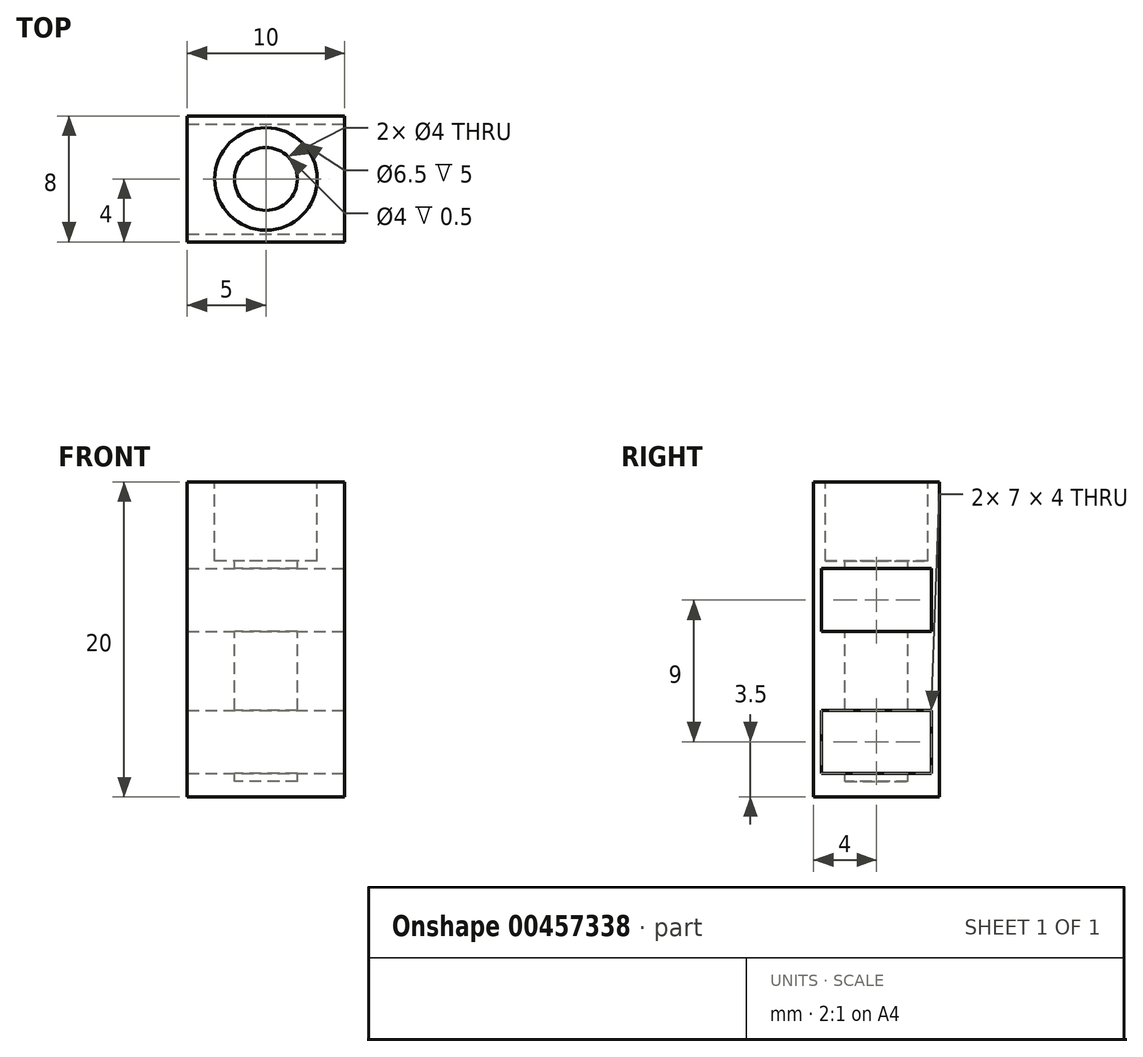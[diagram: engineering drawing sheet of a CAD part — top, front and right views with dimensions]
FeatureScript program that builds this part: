
annotation { "Feature Type Name" : "Feature", "Feature Type Description" : "" }
export const myFeature = defineFeature(function(context is Context, id is Id, definition is map)
    precondition{}
    {
        {
            var Q0;
            Q0=qCreatedBy(makeId("Front.planeOp"),FACE);
            var sketch = newSketch(context, id + "F0", { "sketchPlane" : qUnion([Q0])});
            skLineSegment(sketch, "E0.bottom", {"start": v(-7.5, 10) * mm, "end": v(7.5, 10) * mm});
            skLineSegment(sketch, "E0.top", {"start": v(-7.5, -10) * mm, "end": v(7.5, -10) * mm});
            skLineSegment(sketch, "E0.left", {"start": v(-7.5, 10) * mm, "end": v(-7.5, -10) * mm});
            skLineSegment(sketch, "E0.right", {"start": v(7.5, 10) * mm, "end": v(7.5, -10) * mm});
            skPoint(sketch, "E0.middle", {"position": v(0, 0) * mm});
            skSolve(sketch);
        }
        {
            var Q0;
            Q0 = qSketchRegion(id + "F0", true);
            extrude(context, id + "F1", {"entities" : qUnion([Q0]), "endBound" : BoundingType.SYMMETRIC, "depth" : 8 * mm});
        }
        {
            var Q0;
            Q0=makeQuery(id+"F1.opExtrude","SWEPT_FACE",FACE,{"disambiguationData":[OSD([sQuery(id+"F0.wireOp",EDGE,"E0.bottom")])]});
            var sketch = newSketch(context, id + "F2", { "sketchPlane" : qUnion([Q0])});
            skCircle(sketch, "E1", {"center": v(-2.5, 0) * mm, "radius": 2 * mm});
            skPoint(sketch, "E1.centerSnap0", {"position": v(-7.5, 0) * mm});
            skSolve(sketch);
        }
        {
            var Q0;
            Q0 = qSketchRegion(id + "F2", true);
            extrude(context, id + "F3", {"entities" : qUnion([Q0]), "operationType" : NewBodyOperationType.REMOVE, "oppositeDirection" : true, "depth" : 19 * mm});
        }
        {
            var Q0;
            Q0=makeQuery(id+"F1.opExtrude","SWEPT_FACE",FACE,{"disambiguationData":[OSD([sQuery(id+"F0.wireOp",EDGE,"E0.bottom")])]});
            var sketch = newSketch(context, id + "F4", { "sketchPlane" : qUnion([Q0])});
            skCircle(sketch, "E2", {"center": v(-2.5, 0) * mm, "radius": 3.25 * mm});
            skSolve(sketch);
        }
        {
            var Q0;
            Q0=makeQuery(id+"F4.imprint","IMPRINT",FACE,{"disambiguationData":[TD([[makeQuery(id+"F4.imprint","IMPRINT",EDGE,{"derivedFrom":sQuery(id+"F4.wireOp",EDGE,"E2")}),1.0]])]});
            extrude(context, id + "F5", {"entities" : qUnion([Q0]), "operationType" : NewBodyOperationType.REMOVE, "oppositeDirection" : true, "depth" : 5 * mm});
        }
        {
            var Q0;
            Q0=makeQuery(id+"F1.opExtrude","SWEPT_FACE",FACE,{"disambiguationData":[OSD([sQuery(id+"F0.wireOp",EDGE,"E0.right")])]});
            var sketch = newSketch(context, id + "F6", { "sketchPlane" : qUnion([Q0])});
            skLineSegment(sketch, "E3.bottom", {"start": v(3.5, -4.5) * mm, "end": v(-3.5, -4.5) * mm});
            skLineSegment(sketch, "E3.top", {"start": v(3.5, -8.5) * mm, "end": v(-3.5, -8.5) * mm});
            skLineSegment(sketch, "E3.left", {"start": v(3.5, -4.5) * mm, "end": v(3.5, -8.5) * mm});
            skLineSegment(sketch, "E3.right", {"start": v(-3.5, -4.5) * mm, "end": v(-3.5, -8.5) * mm});
            skPoint(sketch, "E3.middle", {"position": v(0, -6.5) * mm});
            skPoint(sketch, "E4", {"position": v(0, -10) * mm});
            skLineSegment(sketch, "E5.0.1.0", {"start": v(3.5, 4.5) * mm, "end": v(-3.5, 4.5) * mm});
            skLineSegment(sketch, "E5.0.1.1", {"start": v(-3.5, 4.5) * mm, "end": v(-3.5, 0.5) * mm});
            skLineSegment(sketch, "E5.0.1.2", {"start": v(3.5, 0.5) * mm, "end": v(-3.5, 0.5) * mm});
            skLineSegment(sketch, "E5.0.1.3", {"start": v(3.5, 4.5) * mm, "end": v(3.5, 0.5) * mm});
            skPoint(sketch, "E5.0.1.4", {"position": v(0, 2.5) * mm});
            skLineSegment(sketch, "E5.direction1", {"start": v(-3.5, -4.5) * mm, "end": v(22, -4.5) * mm, "construction": true});
            skLineSegment(sketch, "E5.direction2", {"start": v(-3.5, -4.5) * mm, "end": v(-3.5, 4.5) * mm, "construction": true});
            skSolve(sketch);
        }
        {
            var Q0;
            Q0=makeQuery(id+"F6.imprint","IMPRINT",FACE,{"disambiguationData":[TD([[makeQuery(id+"F6.imprint","IMPRINT",EDGE,{"derivedFrom":sQuery(id+"F6.wireOp",EDGE,"E5.0.1.0")}),1.0]])]});
            var Q1;
            Q1=makeQuery(id+"F6.imprint","IMPRINT",FACE,{"disambiguationData":[TD([[makeQuery(id+"F6.imprint","IMPRINT",EDGE,{"derivedFrom":sQuery(id+"F6.wireOp",EDGE,"E3.bottom")}),1.0]])]});
            extrude(context, id + "F7", {"entities" : qUnion([Q0, Q1]), "operationType" : NewBodyOperationType.REMOVE, "endBound" : BoundingType.THROUGH_ALL, "oppositeDirection" : true, "depth" : 14 * mm});
        }
        {
            var Q0;
            Q0=makeQuery(id+"F1.opExtrude","CAP_FACE",FACE,{"disambiguationData":[OSD([sQuery(id+"F0.wireOp",EDGE,"E0.bottom"),sQuery(id+"F0.wireOp",EDGE,"E0.top"),sQuery(id+"F0.wireOp",EDGE,"E0.left"),sQuery(id+"F0.wireOp",EDGE,"E0.right")])],"isStart":false});
            var sketch = newSketch(context, id + "F8", { "sketchPlane" : qUnion([Q0])});
            skLineSegment(sketch, "E6.bottom", {"start": v(7.5, 10) * mm, "end": v(2.5, 10) * mm});
            skLineSegment(sketch, "E6.top", {"start": v(7.5, -10) * mm, "end": v(2.5, -10) * mm});
            skLineSegment(sketch, "E6.left", {"start": v(7.5, 10) * mm, "end": v(7.5, -10) * mm});
            skLineSegment(sketch, "E6.right", {"start": v(2.5, 10) * mm, "end": v(2.5, -10) * mm});
            skSolve(sketch);
        }
        {
            var Q0;
            Q0=makeQuery(id+"F8.imprint","IMPRINT",FACE,{"disambiguationData":[TD([[makeQuery(id+"F8.imprint","IMPRINT",EDGE,{"derivedFrom":sQuery(id+"F8.wireOp",EDGE,"E6.bottom")}),-1.0]])]});
            extrude(context, id + "F9", {"entities" : qUnion([Q0]), "operationType" : NewBodyOperationType.REMOVE, "endBound" : BoundingType.THROUGH_ALL, "oppositeDirection" : true, "depth" : 25 * mm});
        }
    });
